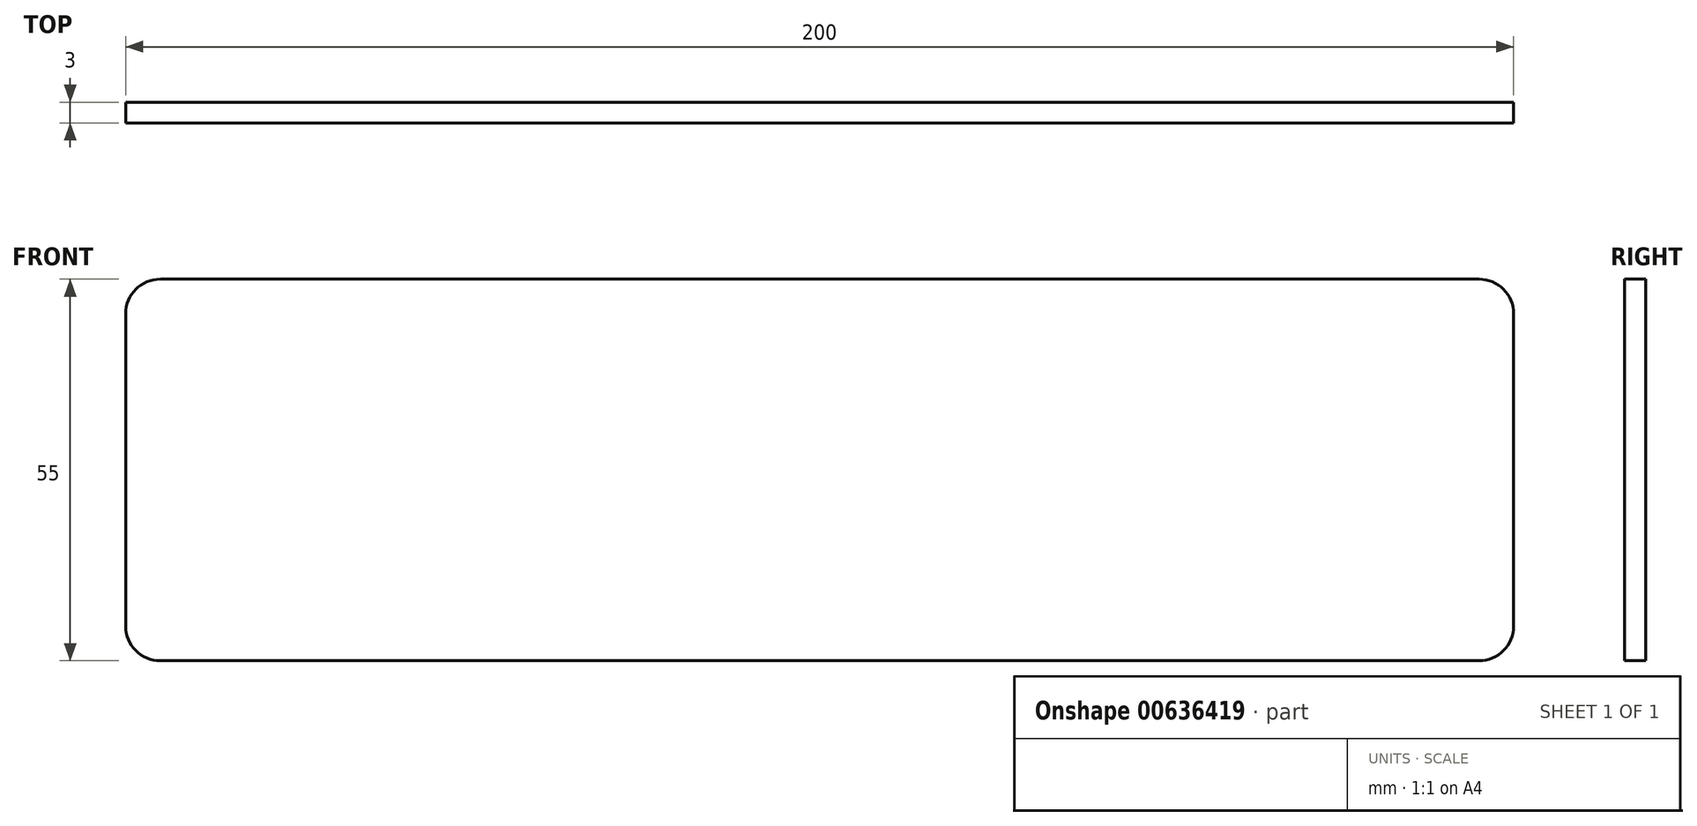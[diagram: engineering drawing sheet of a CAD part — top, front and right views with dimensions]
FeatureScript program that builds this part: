
annotation { "Feature Type Name" : "Feature", "Feature Type Description" : "" }
export const myFeature = defineFeature(function(context is Context, id is Id, definition is map)
    precondition{}
    {
        {
            var Q0;
            Q0=qCreatedBy(makeId("Front.planeOp"),FACE);
            var sketch = newSketch(context, id + "F0", { "sketchPlane" : qUnion([Q0])});
            skLineSegment(sketch, "E0.bottom", {"start": v(-56.44, 28.7) * mm, "end": v(133.56, 28.7) * mm});
            skLineSegment(sketch, "E0.top", {"start": v(-56.44, -26.3) * mm, "end": v(133.56, -26.3) * mm});
            skLineSegment(sketch, "E0.left", {"start": v(-61.44, 23.7) * mm, "end": v(-61.44, -21.3) * mm});
            skLineSegment(sketch, "E0.right", {"start": v(138.56, 23.7) * mm, "end": v(138.56, -21.3) * mm});
            skPoint(sketch, "E1.visualSharp", {"position": v(-61.44, 28.7) * mm});
            skArc(sketch, "E1.filletArc", {"start": v(-56.44, 28.7) * mm, "mid": v(-59.97, 27.24) * mm, "end": v(-61.44, 23.7) * mm});
            skPoint(sketch, "E2.visualSharp", {"position": v(138.56, 28.7) * mm});
            skArc(sketch, "E2.filletArc", {"start": v(138.56, 23.7) * mm, "mid": v(137.1, 27.24) * mm, "end": v(133.56, 28.7) * mm});
            skPoint(sketch, "E3.visualSharp", {"position": v(138.56, -26.3) * mm});
            skArc(sketch, "E3.filletArc", {"start": v(133.56, -26.3) * mm, "mid": v(137.1, -24.83) * mm, "end": v(138.56, -21.3) * mm});
            skPoint(sketch, "E4.visualSharp", {"position": v(-61.44, -26.3) * mm});
            skArc(sketch, "E4.filletArc", {"start": v(-61.44, -21.3) * mm, "mid": v(-59.97, -24.83) * mm, "end": v(-56.44, -26.3) * mm});
            skSolve(sketch);
        }
        {
            var Q0;
            Q0=makeQuery(id+"F0.imprint","IMPRINT",FACE,{"disambiguationData":[TD([[makeQuery(id+"F0.imprint","IMPRINT",EDGE,{"derivedFrom":sQuery(id+"F0.wireOp",EDGE,"E0.bottom")}),-1.0]])]});
            extrude(context, id + "F1", {"entities" : qUnion([Q0]), "depth" : 3 * mm, "offsetDistance" : 25 * mm});
        }
    });
